# Revit family: РВК-Угольник комбинированный с креплением НР
name_source: partatom
category: Арматура трубопроводов
revit_build: Autodesk Revit 2016 (Build: 20150714_1515(x64)
units: mm (PartAtom-declared; Revit-internal decimal feet)

## family parameters
Всегда вертикально = Да
На основе рабочей плоскости = Нет
Общий = Нет
При загрузке вырезать с полостями = Нет
Размер круглого соединителя = Использовать радиус
Тип детали = Нормальный

## types (2) — shared parameters
ADSK_Завод-изготовитель = РВК
B = 29 мм
E = 36 мм
F = 21 мм
G = 20 мм
H = 12 мм
I = 14 мм
J = 47 мм
K = 62 мм
L1 = 27 мм
L2 = 31 мм
N = 15 мм
P = 20 мм
P/2 = 10 мм
Q = 11 мм
S = 6 мм
g = 10 мм
Материал стальной части = РВК_Сталь хромированная
Материал фитинга = РВК_Полипропилен PPR

## per-type parameters (varying)
| type | A | C | D | DN | L1-A | r |
| Угольник комбинированный с креплением ПП D16-1/2'' НР | 14 мм | 11 мм | 16 мм | 16 мм | 13 мм | 8 мм |
| Угольник комбинированный с креплением ПП D20-1/2'' НР | 16 мм | 16 мм | 20 мм | 20 мм | 12 мм | 10 мм |

note: column(s) folded — value = type name in every type: Type

## geometry (parser evidence)
native form markers: Blend x4
no freeform markers — native parametric forms only
